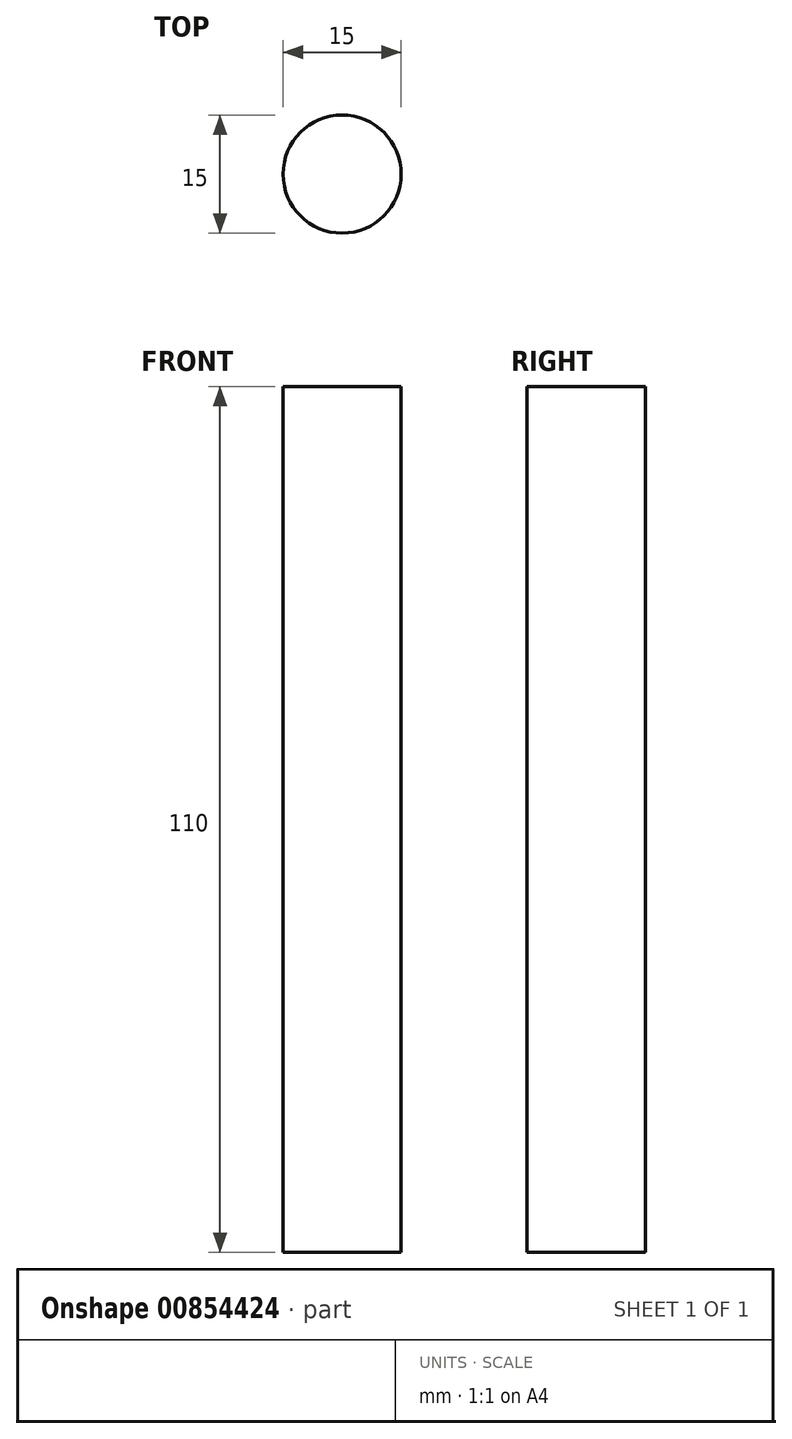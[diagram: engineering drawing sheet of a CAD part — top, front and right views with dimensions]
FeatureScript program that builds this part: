
annotation { "Feature Type Name" : "Feature", "Feature Type Description" : "" }
export const myFeature = defineFeature(function(context is Context, id is Id, definition is map)
    precondition{}
    {
        {
            var Q0;
            Q0=qCreatedBy(makeId("Top.planeOp"),FACE);
            var sketch = newSketch(context, id + "F0", { "sketchPlane" : qUnion([Q0])});
            skCircle(sketch, "E0", {"center": v(0, 0) * mm, "radius": 7.5 * mm});
            skSolve(sketch);
        }
        {
            var Q0;
            Q0=sQuery(id+"F0.wireOp",EDGE,"E0");
            extrude(context, id + "F1", {"bodyType" : ToolBodyType.SURFACE, "surfaceEntities" : qUnion([Q0]), "depth" : 110 * mm, "offsetDistance" : 25 * mm});
        }
    });
